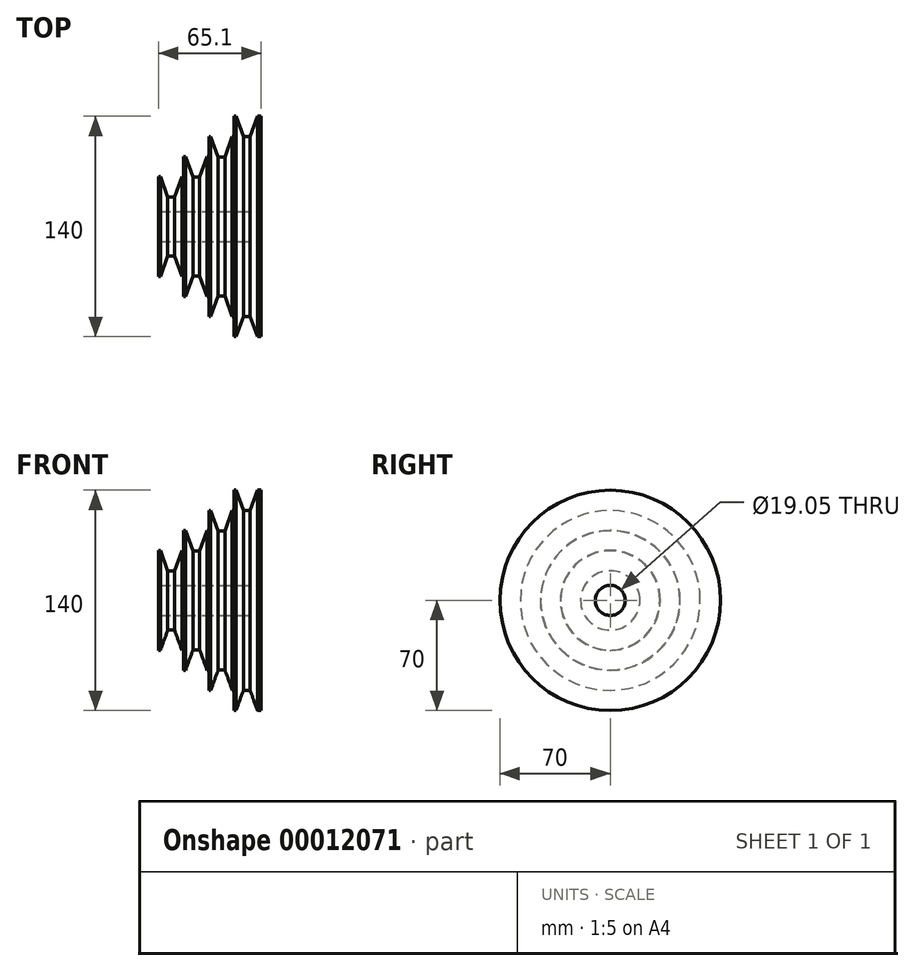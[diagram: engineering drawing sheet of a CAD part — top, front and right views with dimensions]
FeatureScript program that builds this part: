
annotation { "Feature Type Name" : "Feature", "Feature Type Description" : "" }
export const myFeature = defineFeature(function(context is Context, id is Id, definition is map)
    precondition{}
    {
        {
            var Q0;
            Q0=qCreatedBy(makeId("Front.planeOp"),FACE);
            var sketch = newSketch(context, id + "F0", { "sketchPlane" : qUnion([Q0])});
            skLineSegment(sketch, "E0.bottom", {"start": v(0, 0) * mm, "end": v(-65.1, 0) * mm, "construction": true});
            skLineSegment(sketch, "E0.left", {"start": v(0, 9.52) * mm, "end": v(0, 70) * mm});
            skLineSegment(sketch, "E1", {"start": v(-43.25, 31.5) * mm, "end": v(-38.95, 31.5) * mm});
            skLineSegment(sketch, "E2", {"start": v(-43.25, 31.5) * mm, "end": v(-47.95, 44.4) * mm});
            skLineSegment(sketch, "E3", {"start": v(-38.95, 31.5) * mm, "end": v(-34.25, 44.4) * mm});
            skLineSegment(sketch, "E4", {"start": v(-49.1, 44.4) * mm, "end": v(-47.95, 44.4) * mm});
            skLineSegment(sketch, "E5.trimOffspring", {"start": v(-34.25, 44.4) * mm, "end": v(-33.1, 44.4) * mm});
            skPoint(sketch, "E6.start.orphan", {"position": v(-41.1, 31.5) * mm});
            skPoint(sketch, "E7.orphan", {"position": v(-41.1, 44.4) * mm});
            skLineSegment(sketch, "E8", {"start": v(-59.25, 18.85) * mm, "end": v(-54.95, 18.85) * mm});
            skLineSegment(sketch, "E9", {"start": v(-59.25, 18.85) * mm, "end": v(-63.95, 31.75) * mm});
            skLineSegment(sketch, "E10", {"start": v(-54.95, 18.85) * mm, "end": v(-50.25, 31.75) * mm});
            skLineSegment(sketch, "E11", {"start": v(-65.1, 31.75) * mm, "end": v(-63.95, 31.75) * mm});
            skLineSegment(sketch, "E12.trimOffspring", {"start": v(-50.25, 31.75) * mm, "end": v(-49.1, 31.75) * mm});
            skPoint(sketch, "E13.start.orphan", {"position": v(-57.1, 18.85) * mm});
            skPoint(sketch, "E14.orphan", {"position": v(-57.1, 31.75) * mm});
            skLineSegment(sketch, "E15", {"start": v(-11.25, 57.1) * mm, "end": v(-6.95, 57.1) * mm});
            skLineSegment(sketch, "E16", {"start": v(-11.25, 57.1) * mm, "end": v(-15.94, 70) * mm});
            skLineSegment(sketch, "E17", {"start": v(-6.95, 57.1) * mm, "end": v(-2.25, 70) * mm});
            skLineSegment(sketch, "E18", {"start": v(-17.1, 70) * mm, "end": v(-15.94, 70) * mm});
            skPoint(sketch, "E19.start.orphan", {"position": v(-9.1, 57.1) * mm});
            skPoint(sketch, "E20.orphan", {"position": v(-9.1, 70) * mm});
            skLineSegment(sketch, "E21", {"start": v(-27.25, 44.2) * mm, "end": v(-22.95, 44.2) * mm});
            skLineSegment(sketch, "E22", {"start": v(-27.25, 44.2) * mm, "end": v(-31.95, 57.1) * mm});
            skLineSegment(sketch, "E23", {"start": v(-22.95, 44.2) * mm, "end": v(-18.25, 57.1) * mm});
            skLineSegment(sketch, "E24", {"start": v(-33.1, 57.1) * mm, "end": v(-31.95, 57.1) * mm});
            skLineSegment(sketch, "E25.trimOffspring", {"start": v(-18.25, 57.1) * mm, "end": v(-17.1, 57.1) * mm});
            skPoint(sketch, "E26.start.orphan", {"position": v(-25.1, 44.2) * mm});
            skPoint(sketch, "E27.orphan", {"position": v(-25.1, 57.1) * mm});
            skLineSegment(sketch, "E28", {"start": v(-65.1, 31.75) * mm, "end": v(-65.1, 9.53) * mm});
            skLineSegment(sketch, "E29", {"start": v(-49.1, 44.4) * mm, "end": v(-49.1, 31.75) * mm});
            skLineSegment(sketch, "E30", {"start": v(-33.1, 57.1) * mm, "end": v(-33.1, 44.4) * mm});
            skLineSegment(sketch, "E31", {"start": v(-17.1, 70) * mm, "end": v(-17.1, 57.1) * mm});
            skLineSegment(sketch, "E32", {"start": v(-2.25, 70) * mm, "end": v(0, 70) * mm});
            skLineSegment(sketch, "E33.0", {"start": v(0, 9.53) * mm, "end": v(-65.1, 9.53) * mm});
            skSolve(sketch);
        }
        {
            var Q0;
            Q0 = qSketchRegion(id + "F0", true);
            var Q1;
            Q1=sQuery(id+"F0.wireOp",EDGE,"E0.bottom");
            revolve(context, id + "F1", {"entities" : qUnion([Q0]), "axis" : qUnion([Q1]), "revolveType" : RevolveType.FULL});
        }
    });
